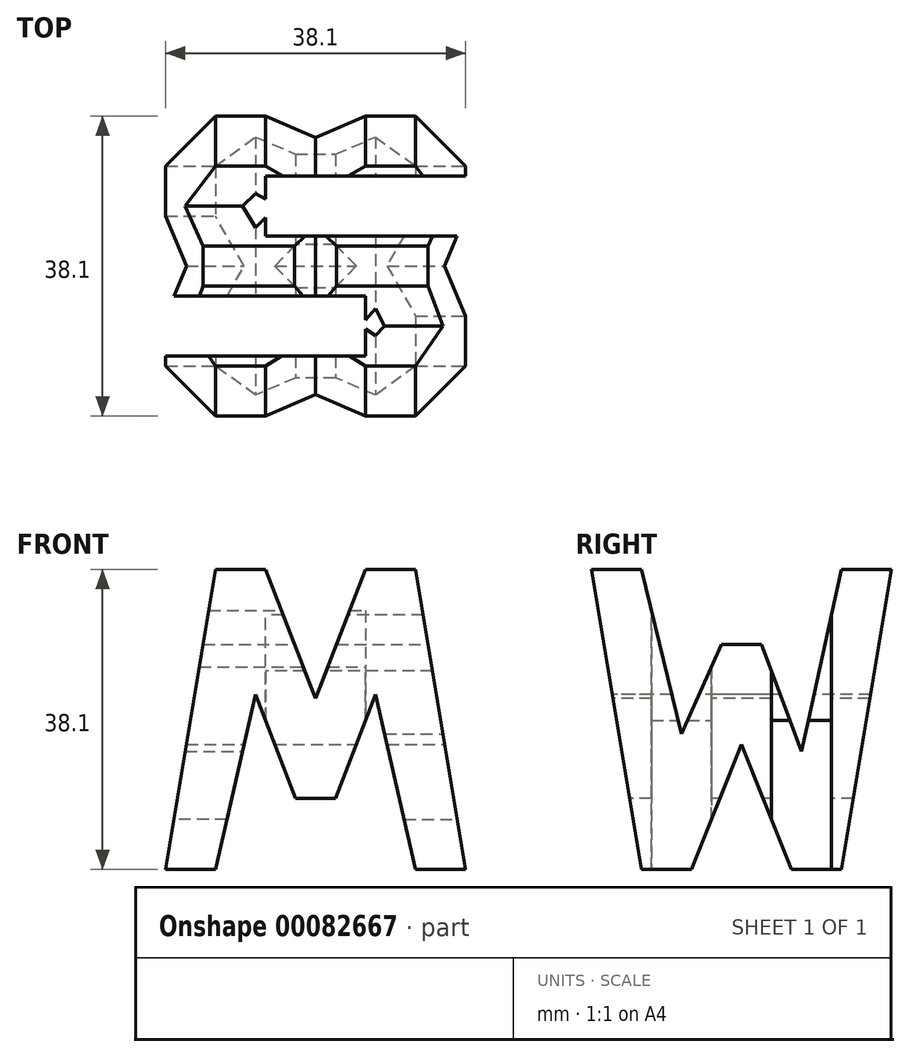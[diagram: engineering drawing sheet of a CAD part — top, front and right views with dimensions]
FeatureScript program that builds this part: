
annotation { "Feature Type Name" : "Feature", "Feature Type Description" : "" }
export const myFeature = defineFeature(function(context is Context, id is Id, definition is map)
    precondition{}
    {
        {
            var Q0;
            Q0=qCreatedBy(makeId("Front.planeOp"),FACE);
            var sketch = newSketch(context, id + "F0", { "sketchPlane" : qUnion([Q0])});
            skLineSegment(sketch, "E0", {"start": v(0, 0) * mm, "end": v(38.1, 0) * mm});
            skLineSegment(sketch, "E1", {"start": v(38.1, 38.1) * mm, "end": v(38.1, 0) * mm});
            skLineSegment(sketch, "E2", {"start": v(38.1, 38.1) * mm, "end": v(0, 38.1) * mm});
            skLineSegment(sketch, "E3", {"start": v(0, 38.1) * mm, "end": v(0, 0) * mm});
            skSolve(sketch);
        }
        {
            var Q0;
            Q0 = qSketchRegion(id + "F0", true);
            extrude(context, id + "F1", {"entities" : qUnion([Q0]), "depth" : 38.1 * mm});
        }
        {
            var Q0;
            Q0=qCreatedBy(makeId("Front.planeOp"),FACE);
            cPlane(context, id + "F2", {"entities" : qUnion([Q0]), "cplaneType" : CPlaneType.OFFSET, "offset" : 38.1 * mm, "width" : 152.4 * mm, "height" : 152.4 * mm});
        }
        {
            var Q0;
            Q0=qCreatedBy(makeId("Right.planeOp"),FACE);
            cPlane(context, id + "F3", {"entities" : qUnion([Q0]), "cplaneType" : CPlaneType.OFFSET, "offset" : 38.1 * mm, "width" : 152.4 * mm, "height" : 152.4 * mm});
        }
        {
            var Q0;
            Q0=qCreatedBy(makeId("Top.planeOp"),FACE);
            cPlane(context, id + "F4", {"entities" : qUnion([Q0]), "cplaneType" : CPlaneType.OFFSET, "offset" : 38.1 * mm, "width" : 152.4 * mm, "height" : 152.4 * mm});
        }
        {
            var Q0;
            Q0=qCreatedBy(id+"F3.planeOp",FACE);
            var sketch = newSketch(context, id + "F5", { "sketchPlane" : qUnion([Q0])});
            skLineSegment(sketch, "E4", {"start": v(0, 38.1) * mm, "end": v(-6.35, 38.1) * mm});
            skLineSegment(sketch, "E5", {"start": v(-31.75, 0) * mm, "end": v(-25.4, 0) * mm});
            skLineSegment(sketch, "E6", {"start": v(-6.35, 0) * mm, "end": v(-12.7, 0) * mm});
            skLineSegment(sketch, "E7", {"start": v(-31.75, 38.1) * mm, "end": v(-26.67, 17.24) * mm});
            skLineSegment(sketch, "E8", {"start": v(-26.67, 17.24) * mm, "end": v(-21.59, 28.58) * mm});
            skLineSegment(sketch, "E9", {"start": v(-21.59, 28.58) * mm, "end": v(-16.5, 28.58) * mm});
            skLineSegment(sketch, "E10", {"start": v(-16.5, 28.58) * mm, "end": v(-11.43, 15.01) * mm});
            skLineSegment(sketch, "E11", {"start": v(-11.43, 15.01) * mm, "end": v(-6.35, 38.1) * mm});
            skLineSegment(sketch, "E12", {"start": v(-6.35, 38.1) * mm, "end": v(0, 38.1) * mm});
            skLineSegment(sketch, "E13", {"start": v(0, 38.1) * mm, "end": v(-6.35, 0) * mm});
            skLineSegment(sketch, "E14", {"start": v(-12.7, 0) * mm, "end": v(-19.05, 15.88) * mm});
            skLineSegment(sketch, "E15", {"start": v(-19.05, 15.88) * mm, "end": v(-25.4, 0) * mm});
            skLineSegment(sketch, "E16", {"start": v(-25.4, 0) * mm, "end": v(-31.75, 0) * mm});
            skLineSegment(sketch, "E17", {"start": v(-31.75, 0) * mm, "end": v(-38.1, 38.1) * mm});
            skLineSegment(sketch, "E18.trimOffspring", {"start": v(-31.75, 38.1) * mm, "end": v(-38.1, 38.1) * mm});
            skLineSegment(sketch, "E19.trimOffspring", {"start": v(-12.7, 0) * mm, "end": v(-6.35, 0) * mm});
            skPoint(sketch, "E20.orphan", {"position": v(-41.13, 0) * mm});
            skLineSegment(sketch, "E21.bottom", {"start": v(0, 0) * mm, "end": v(-38.1, 0) * mm});
            skLineSegment(sketch, "E21.top", {"start": v(0, 38.1) * mm, "end": v(-38.1, 38.1) * mm});
            skLineSegment(sketch, "E21.left", {"start": v(0, 0) * mm, "end": v(0, 38.1) * mm});
            skLineSegment(sketch, "E21.right", {"start": v(-38.1, 0) * mm, "end": v(-38.1, 38.1) * mm});
            skSolve(sketch);
        }
        {
            var Q0;
            {var subQ0=sQuery(id+"F5.wireOp",EDGE,"E7");Q0=makeQuery(id+"F5.imprint","IMPRINT",FACE,{"disambiguationData":[TD([[makeQuery(id+"F5.imprint","IMPRINT",EDGE,{"derivedFrom":subQ0}),1.0]])]});}
            var Q1;
            {var subQ0=sQuery(id+"F5.wireOp",EDGE,"E13");Q1=makeQuery(id+"F5.imprint","IMPRINT",FACE,{"disambiguationData":[TD([[makeQuery(id+"F5.imprint","IMPRINT",EDGE,{"derivedFrom":subQ0}),1.0]])]});}
            var Q2;
            {var subQ0=sQuery(id+"F5.wireOp",EDGE,"E14");Q2=makeQuery(id+"F5.imprint","IMPRINT",FACE,{"disambiguationData":[TD([[makeQuery(id+"F5.imprint","IMPRINT",EDGE,{"derivedFrom":subQ0}),1.0]])]});}
            var Q3;
            {var subQ0=sQuery(id+"F5.wireOp",EDGE,"E17");Q3=makeQuery(id+"F5.imprint","IMPRINT",FACE,{"disambiguationData":[TD([[makeQuery(id+"F5.imprint","IMPRINT",EDGE,{"derivedFrom":subQ0}),1.0]])]});}
            extrude(context, id + "F6", {"entities" : qUnion([Q0, Q1, Q2, Q3]), "operationType" : NewBodyOperationType.REMOVE, "oppositeDirection" : true, "depth" : 38.1 * mm});
        }
        {
            var Q0;
            Q0=qCreatedBy(id+"F2.planeOp",FACE);
            var sketch = newSketch(context, id + "F7", { "sketchPlane" : qUnion([Q0])});
            skLineSegment(sketch, "E22", {"start": v(0, 0) * mm, "end": v(0, 38.1) * mm});
            skLineSegment(sketch, "E23", {"start": v(0, 38.1) * mm, "end": v(38.1, 38.1) * mm});
            skLineSegment(sketch, "E24", {"start": v(38.1, 38.1) * mm, "end": v(38.1, 0) * mm});
            skLineSegment(sketch, "E25", {"start": v(38.1, 0) * mm, "end": v(0, 0) * mm});
            skLineSegment(sketch, "E26", {"start": v(6.35, 38.1) * mm, "end": v(0, 0) * mm});
            skLineSegment(sketch, "E27", {"start": v(6.35, 0) * mm, "end": v(11.43, 22.22) * mm});
            skLineSegment(sketch, "E28", {"start": v(11.43, 22.22) * mm, "end": v(16.51, 9) * mm});
            skLineSegment(sketch, "E29", {"start": v(16.51, 9) * mm, "end": v(21.6, 9) * mm});
            skLineSegment(sketch, "E30", {"start": v(21.59, 9) * mm, "end": v(26.67, 22.22) * mm});
            skLineSegment(sketch, "E31", {"start": v(26.67, 22.22) * mm, "end": v(31.75, 0) * mm});
            skLineSegment(sketch, "E32", {"start": v(31.75, 0) * mm, "end": v(38.1, 0) * mm});
            skLineSegment(sketch, "E33", {"start": v(38.1, 0) * mm, "end": v(31.75, 38.1) * mm});
            skLineSegment(sketch, "E34", {"start": v(31.75, 38.1) * mm, "end": v(25.4, 38.1) * mm});
            skLineSegment(sketch, "E35", {"start": v(25.4, 38.1) * mm, "end": v(19.05, 21.7) * mm});
            skLineSegment(sketch, "E36", {"start": v(19.05, 21.7) * mm, "end": v(12.7, 38.1) * mm});
            skSolve(sketch);
        }
        {
            var Q0;
            {var subQ0=sQuery(id+"F7.wireOp",EDGE,"E22");Q0=makeQuery(id+"F7.imprint","IMPRINT",FACE,{"disambiguationData":[TD([[makeQuery(id+"F7.imprint","IMPRINT",EDGE,{"derivedFrom":subQ0}),-1.0]])]});}
            var Q1;
            {var subQ0=sQuery(id+"F7.wireOp",EDGE,"E35");Q1=makeQuery(id+"F7.imprint","IMPRINT",FACE,{"disambiguationData":[TD([[makeQuery(id+"F7.imprint","IMPRINT",EDGE,{"derivedFrom":subQ0}),-1.0]])]});}
            var Q2;
            {var subQ0=sQuery(id+"F7.wireOp",EDGE,"E24");Q2=makeQuery(id+"F7.imprint","IMPRINT",FACE,{"disambiguationData":[TD([[makeQuery(id+"F7.imprint","IMPRINT",EDGE,{"derivedFrom":subQ0}),-1.0]])]});}
            var Q3;
            {var subQ0=sQuery(id+"F7.wireOp",EDGE,"E27");Q3=makeQuery(id+"F7.imprint","IMPRINT",FACE,{"disambiguationData":[TD([[makeQuery(id+"F7.imprint","IMPRINT",EDGE,{"derivedFrom":subQ0}),-1.0]])]});}
            extrude(context, id + "F8", {"entities" : qUnion([Q0, Q1, Q2, Q3]), "operationType" : NewBodyOperationType.REMOVE, "oppositeDirection" : true, "depth" : 38.1 * mm});
        }
        {
            var Q0;
            Q0=qCreatedBy(id+"F4.planeOp",FACE);
            var sketch = newSketch(context, id + "F9", { "sketchPlane" : qUnion([Q0])});
            skLineSegment(sketch, "E37", {"start": v(0, 0) * mm, "end": v(0, -38.1) * mm});
            skLineSegment(sketch, "E38", {"start": v(0, -38.1) * mm, "end": v(38.1, -38.1) * mm});
            skLineSegment(sketch, "E39", {"start": v(38.1, -38.1) * mm, "end": v(38.1, 0) * mm});
            skLineSegment(sketch, "E40", {"start": v(38.1, 0) * mm, "end": v(0, 0) * mm});
            skLineSegment(sketch, "E41", {"start": v(12.7, -7.62) * mm, "end": v(38.1, -7.62) * mm});
            skLineSegment(sketch, "E42", {"start": v(12.7, -7.62) * mm, "end": v(12.7, -15.24) * mm});
            skLineSegment(sketch, "E43", {"start": v(12.7, -15.24) * mm, "end": v(38.1, -15.24) * mm});
            skLineSegment(sketch, "E44", {"start": v(25.4, -22.86) * mm, "end": v(0, -22.86) * mm});
            skLineSegment(sketch, "E45", {"start": v(25.4, -22.86) * mm, "end": v(25.4, -30.48) * mm});
            skLineSegment(sketch, "E46", {"start": v(25.4, -30.48) * mm, "end": v(0, -30.48) * mm});
            skSolve(sketch);
        }
        {
            var Q0;
            {var subQ0=sQuery(id+"F9.wireOp",EDGE,"E44");Q0=makeQuery(id+"F9.imprint","IMPRINT",FACE,{"disambiguationData":[TD([[makeQuery(id+"F9.imprint","IMPRINT",EDGE,{"derivedFrom":subQ0}),1.0]])]});}
            var Q1;
            {var subQ0=sQuery(id+"F9.wireOp",EDGE,"E41");Q1=makeQuery(id+"F9.imprint","IMPRINT",FACE,{"disambiguationData":[TD([[makeQuery(id+"F9.imprint","IMPRINT",EDGE,{"derivedFrom":subQ0}),-1.0]])]});}
            extrude(context, id + "F10", {"entities" : qUnion([Q0, Q1]), "operationType" : NewBodyOperationType.REMOVE, "oppositeDirection" : true, "depth" : 38.1 * mm});
        }
    });
